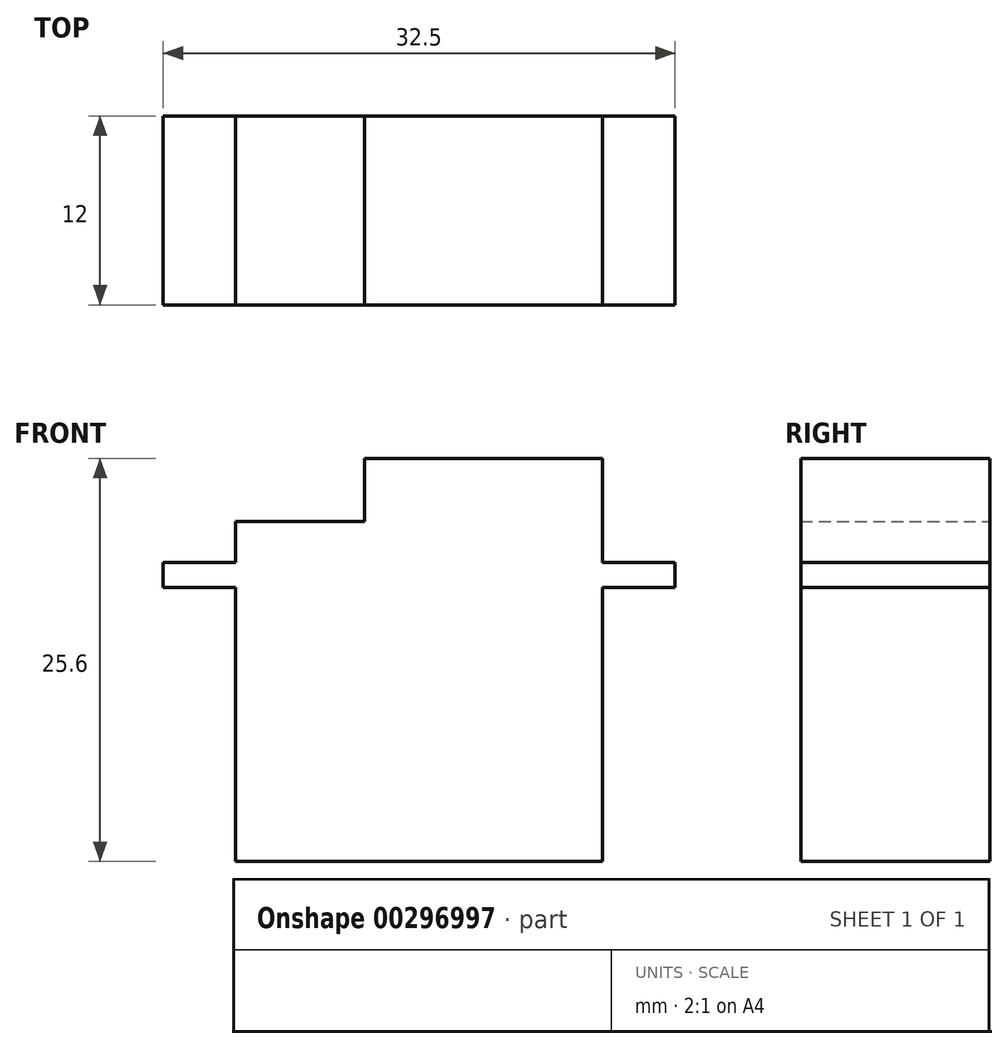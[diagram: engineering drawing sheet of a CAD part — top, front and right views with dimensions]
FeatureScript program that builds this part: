
annotation { "Feature Type Name" : "Feature", "Feature Type Description" : "" }
export const myFeature = defineFeature(function(context is Context, id is Id, definition is map)
    precondition{}
    {
        {
            var Q0;
            Q0=qCreatedBy(makeId("Front.planeOp"),FACE);
            var sketch = newSketch(context, id + "F0", { "sketchPlane" : qUnion([Q0])});
            skLineSegment(sketch, "E0.bottom", {"start": v(0, 4.2) * mm, "end": v(23.3, 4.2) * mm});
            skLineSegment(sketch, "E0.top", {"start": v(0, -17.4) * mm, "end": v(23.3, -17.4) * mm});
            skLineSegment(sketch, "E0.left", {"start": v(0, 4.2) * mm, "end": v(0, -17.4) * mm});
            skLineSegment(sketch, "E0.right", {"start": v(23.3, 4.2) * mm, "end": v(23.3, -17.4) * mm});
            skLineSegment(sketch, "E1.bottom", {"start": v(-4.6, 1.6) * mm, "end": v(27.9, 1.6) * mm});
            skLineSegment(sketch, "E1.top", {"start": v(-4.6, 0) * mm, "end": v(27.9, 0) * mm});
            skLineSegment(sketch, "E1.left", {"start": v(-4.6, 1.6) * mm, "end": v(-4.6, 0) * mm});
            skLineSegment(sketch, "E1.right", {"start": v(27.9, 1.6) * mm, "end": v(27.9, 0) * mm});
            skLineSegment(sketch, "E2.bottom", {"start": v(8.2, 8.2) * mm, "end": v(23.3, 8.2) * mm});
            skLineSegment(sketch, "E2.top", {"start": v(8.2, 4.2) * mm, "end": v(23.3, 4.2) * mm});
            skLineSegment(sketch, "E2.left", {"start": v(8.2, 8.2) * mm, "end": v(8.2, 4.2) * mm});
            skLineSegment(sketch, "E2.right", {"start": v(23.3, 8.2) * mm, "end": v(23.3, 4.2) * mm});
            skLineSegment(sketch, "E3", {"start": v(11.65, -17.4) * mm, "end": v(11.65, 0) * mm, "construction": true});
            skPoint(sketch, "E4", {"position": v(0, 0) * mm});
            skSolve(sketch);
        }
        {
            var Q0;
            {var subQ0=sQuery(id+"F0.wireOp",EDGE,"E0.top");Q0=makeQuery(id+"F0.imprint","IMPRINT",FACE,{"disambiguationData":[TD([[makeQuery(id+"F0.imprint","IMPRINT",EDGE,{"derivedFrom":subQ0}),1.0]])]});}
            var Q1;
            Q1=makeQuery(id+"F0.imprint","IMPRINT",FACE,{"disambiguationData":[TD([[makeQuery(id+"F0.imprint","IMPRINT",EDGE,{"derivedFrom":sQuery(id+"F0.wireOp",EDGE,"E2.bottom")}),-1.0]])]});
            var Q2;
            {var subQ5=sQuery(id+"F0.wireOp",EDGE,"E0.bottom");Q2=makeQuery(id+"F0.imprint","IMPRINT",FACE,{"disambiguationData":[TD([[makeQuery(id+"F0.imprint","IMPRINT",EDGE,{"derivedFrom":subQ5}),-1.0]])]});}
            var Q3;
            {var subQ0=sQuery(id+"F0.wireOp",EDGE,"E1.bottom");var subQ1=sQuery(id+"F0.wireOp",EDGE,"E0.left");var subQ2=makeQuery(id+"F0.imprint","INTERSECT",VERTEX,{"derivedFrom":[subQ1,subQ0]});Q3=makeQuery(id+"F0.imprint","IMPRINT",FACE,{"disambiguationData":[TD([[makeQuery(id+"F0.imprint","IMPRINT",EDGE,{"disambiguationData":[TD([[subQ2,-1.0]])],"derivedFrom":subQ1}),1.0]])]});}
            var Q4;
            {var subQ5=sQuery(id+"F0.wireOp",EDGE,"E1.right");Q4=makeQuery(id+"F0.imprint","IMPRINT",FACE,{"disambiguationData":[TD([[makeQuery(id+"F0.imprint","IMPRINT",EDGE,{"derivedFrom":subQ5}),-1.0]])]});}
            var Q5;
            {var subQ5=sQuery(id+"F0.wireOp",EDGE,"E1.left");Q5=makeQuery(id+"F0.imprint","IMPRINT",FACE,{"disambiguationData":[TD([[makeQuery(id+"F0.imprint","IMPRINT",EDGE,{"derivedFrom":subQ5}),1.0]])]});}
            extrude(context, id + "F1", {"entities" : qUnion([Q0, Q1, Q2, Q3, Q4, Q5]), "depth" : 12 * mm});
        }
    });
